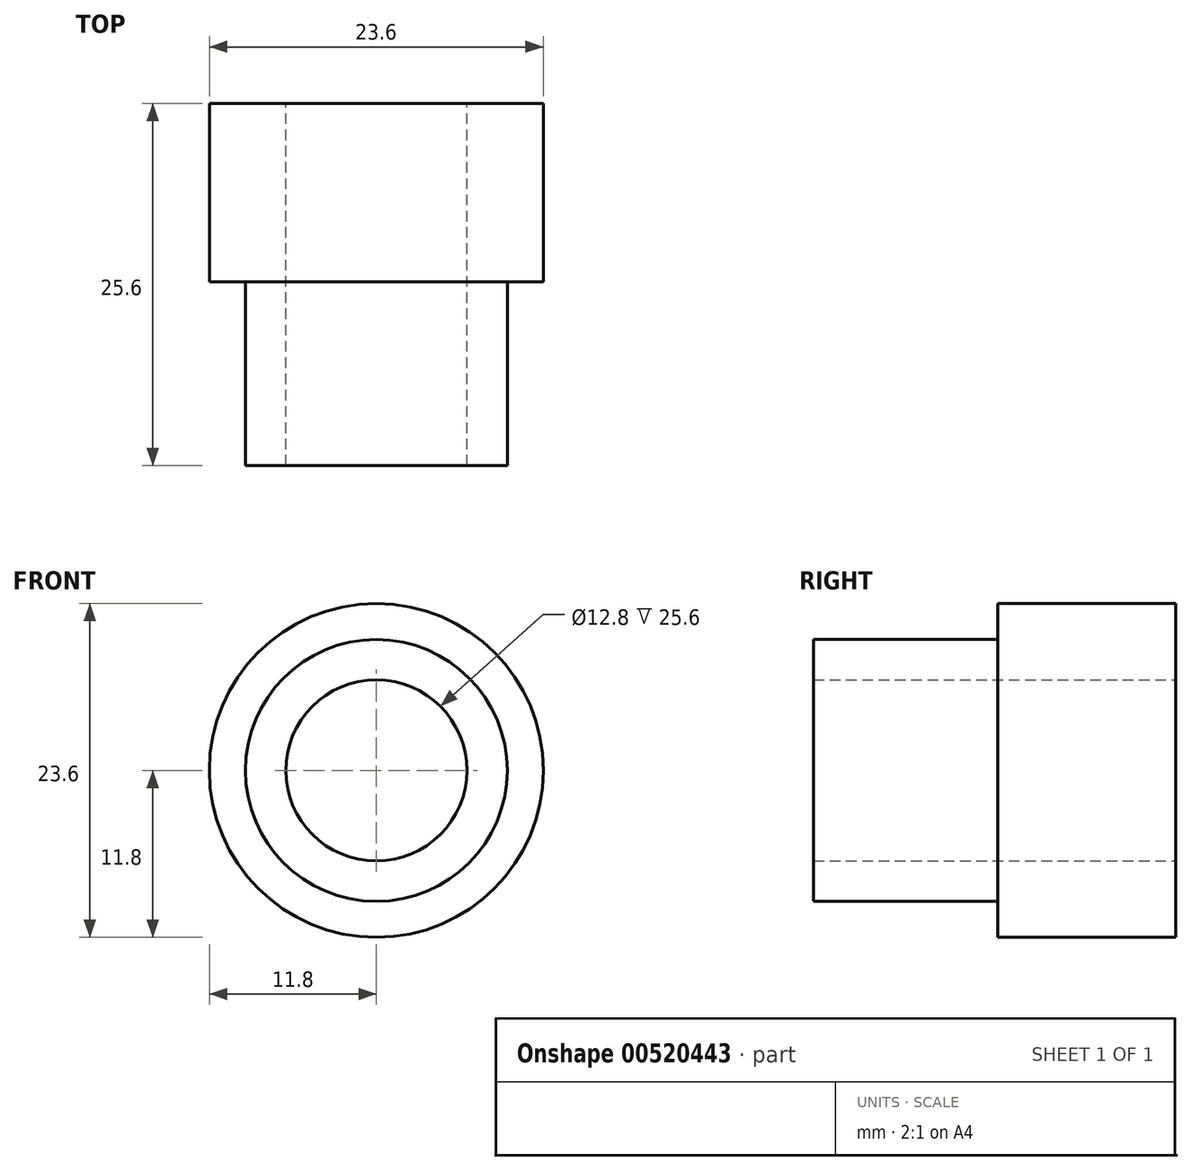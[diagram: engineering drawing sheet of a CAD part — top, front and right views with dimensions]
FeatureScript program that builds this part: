
annotation { "Feature Type Name" : "Feature", "Feature Type Description" : "" }
export const myFeature = defineFeature(function(context is Context, id is Id, definition is map)
    precondition{}
    {
        {
            var Q0;
            Q0=qCreatedBy(makeId("Front.planeOp"),FACE);
            var sketch = newSketch(context, id + "F0", { "sketchPlane" : qUnion([Q0])});
            skCircle(sketch, "E0", {"center": v(0, 0) * mm, "radius": 11.8 * mm});
            skCircle(sketch, "E1", {"center": v(0, 0) * mm, "radius": 6.4 * mm});
            skSolve(sketch);
        }
        {
            var Q0;
            Q0=makeQuery(id+"F0.imprint","IMPRINT",FACE,{"disambiguationData":[TD([[makeQuery(id+"F0.imprint","IMPRINT",EDGE,{"derivedFrom":sQuery(id+"F0.wireOp",EDGE,"E0")}),1.0]])]});
            extrude(context, id + "F1", {"entities" : qUnion([Q0]), "depth" : 25.6 * mm, "offsetDistance" : 25 * mm});
        }
        {
            var Q0;
            Q0=makeQuery(id+"F1.opExtrude","CAP_FACE",FACE,{"disambiguationData":[OSD([sQuery(id+"F0.wireOp",EDGE,"E0"),sQuery(id+"F0.wireOp",EDGE,"E1")])],"isStart":false});
            var sketch = newSketch(context, id + "F2", { "sketchPlane" : qUnion([Q0])});
            skCircle(sketch, "E2", {"center": v(0, 0) * mm, "radius": 9.25 * mm});
            skSolve(sketch);
        }
        {
            var Q0;
            Q0=makeQuery(id+"F2.imprint","IMPRINT",FACE,{"disambiguationData":[TD([[makeQuery(id+"F2.imprint","IMPRINT",EDGE,{"derivedFrom":sQuery(id+"F2.wireOp",EDGE,"E2")}),-1.0]])]});
            extrude(context, id + "F3", {"entities" : qUnion([Q0]), "operationType" : NewBodyOperationType.REMOVE, "oppositeDirection" : true, "depth" : 13 * mm, "offsetDistance" : 25 * mm});
        }
    });
